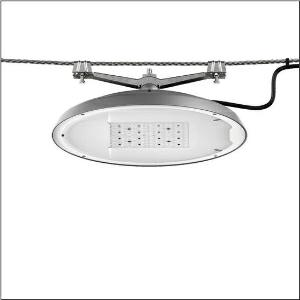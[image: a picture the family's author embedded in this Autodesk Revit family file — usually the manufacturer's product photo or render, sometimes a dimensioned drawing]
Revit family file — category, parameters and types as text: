
# Revit family: dl_r__50_iq_mini___st0_8s_5xa248v41f08le_55a3
name_source: partatom
category: Lighting Fixtures
units: mm (PartAtom-declared; Revit-internal decimal feet)

## family parameters
Cut with Voids When Loaded = No
Host = Face
Light Source = No
Part Type = Normal
Room Calculation Point = No
Round Connector Dimension = Use Diameter
Shared = No

## types (1)
- --- (1 x LED, 10390 lm, 64.1 W, 4000K)
    Apparent Load = 64 VA
    CIE Flux Codes = 38 75 97 100 100
    Color Rendering = 70
    Color Temperature = 4000K
    Default Elevation = 1800 mm
    Description = DL® 50 iQ mini, catenary luminaire, primary light control with lens, of PMMA, primary optical cover: cover, of toughened safety glass, transparent, light distribution: ST0.8s, light emission: direct distribution, primary light characteristic: symmetric, installation type: suspended mounting, LED, High Power LED, rated luminous flux: 10.390lm, luminous efficacy: 162lm/W, light colour: 740, colour temperature: 4000K, control: optimised constant luminous flux control (CLO 2.0), Desk-Remote (wireless, voltage-free reading and setting of iQ features in the workshop via application-optimized NFC function/RFID function), Light-Fading, Smart-Wire, Night-Set, Lumen-Switch, Temp-Guard, Auto-Match, Street-Remote, mains connection: 230..240V, AC, 50/60Hz, start of lifetime: 64W, end of service life: 67W, reduction: 30W, luminaire housing, of diecast aluminium, powder-coated, Siteco® metallic grey (DB 702S), diameter: 500mm, height: 115mm, protection rating (complete): IP66, insulation class (complete): insulation class II (safety insulation), certification: CE, ENEC, VDE, impact resistance: IK08, permissible operating ambient temperature for outdoor applications: -25..+40°C, standard-compliant lighting for roads and squares, packaging unit: 1 piece

Light Distribution: ST0.8s
    Height = 124 mm  [stored 0.406824 ft]
    Lamp = 1 x LED
    Lamp Light Flux = 10390 lm
    Lamp Power = 64.1 W
    Lamp count = 1
    Length = 500 mm
    Luminous efficacy = 162 lm/W
    Manufacturer = Siteco
    ModVariant = No
    Model = 5XA248V41F08LE
    Number of Poles = 1
    OnlyDefault = Yes
    Power Factor = 1
    Product Name = DL® 50 iQ mini | ST0.8s
    Product group = catenary luminaire
    ProductGroupID = 6300
    Protection Class = Protection class II
    Protection Degree = IP 66
    RLX_Detail_Level = 1
    RLX_Emergency_Light_Flux = 0 lm
    RLX_Emergency_Type = 0
    RLX_Emergency_Type_DB = No
    RlxData = <blob elided: 126837 chars, md5=8ab5834b>
    Socket = socket
    Standby Power = 0 W
    System Light Flux = 10390 lm
    System Power = 64 W
    Type Comments = factory setting: luminous flux: 100 % | dim-lin: 254 | 672 mA
    Type Image = l_1251783.jpg
    URL = http://relux.com
    VarID = @adj_090389
    Voltage = 0 V
    Weight = 0.00 kg
    Width = 0 mm  [stored 0 ft]

note: [stored X ft] marks values corroborated as IEEE doubles in the binary element streams (Revit-internal decimal feet)

## geometry (parser evidence)
native form markers: Blend x4, Sweep x13
no freeform markers — native parametric forms only
